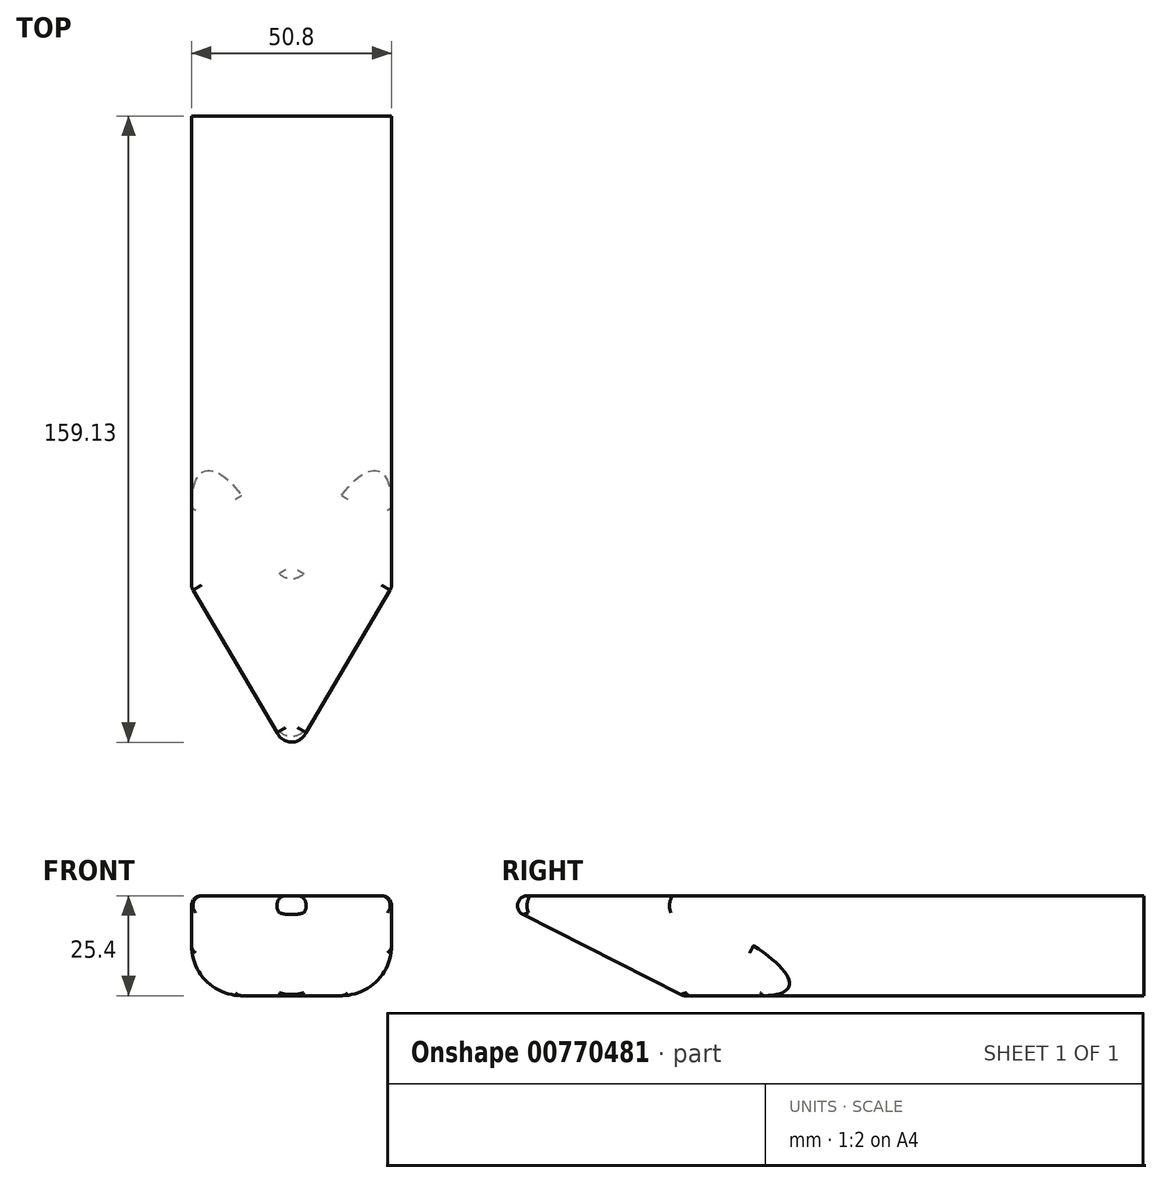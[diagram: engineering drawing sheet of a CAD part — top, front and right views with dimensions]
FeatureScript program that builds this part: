
annotation { "Feature Type Name" : "Feature", "Feature Type Description" : "" }
export const myFeature = defineFeature(function(context is Context, id is Id, definition is map)
    precondition{}
    {
        {
            var Q0;
            Q0=qCreatedBy(makeId("Top.planeOp"),FACE);
            var sketch = newSketch(context, id + "F0", { "sketchPlane" : qUnion([Q0])});
            skLineSegment(sketch, "E0.bottom", {"start": v(25.4, 63.5) * mm, "end": v(-25.4, 63.5) * mm});
            skLineSegment(sketch, "E0.top", {"start": v(25.4, -63.5) * mm, "end": v(-25.4, -63.5) * mm});
            skLineSegment(sketch, "E0.left", {"start": v(25.4, 63.5) * mm, "end": v(25.4, -63.5) * mm});
            skLineSegment(sketch, "E0.right", {"start": v(-25.4, 63.5) * mm, "end": v(-25.4, -63.5) * mm});
            skPoint(sketch, "E0.middle", {"position": v(0, 0) * mm});
            skLineSegment(sketch, "E1", {"start": v(-25.4, -63.5) * mm, "end": v(0, -106.64) * mm});
            skLineSegment(sketch, "E2", {"start": v(0, -106.64) * mm, "end": v(25.4, -63.5) * mm});
            skSolve(sketch);
        }
        {
            var Q0;
            Q0 = qSketchRegion(id + "F0", true);
            extrude(context, id + "F1", {"entities" : qUnion([Q0]), "depth" : 25.4 * mm, "offsetDistance" : 25.4 * mm});
        }
        {
            var Q0;
            Q0=makeQuery(id+"F1.opExtrude","CAP_EDGE",EDGE,{"disambiguationData":[OSD([sQuery(id+"F0.wireOp",EDGE,"E2")])],"isStart":true});
            var Q1;
            Q1=makeQuery(id+"F1.opExtrude","CAP_EDGE",EDGE,{"disambiguationData":[OSD([sQuery(id+"F0.wireOp",EDGE,"E1")])],"isStart":true});
            chamfer(context, id + "F2", {"entities" : qUnion([Q0, Q1]), "width" : 25.4 * mm, "tangentPropagation" : true});
        }
        {
            var Q0;
            Q0=makeQuery(id+"F2.opChamfer","BLEND_EDGE",EDGE,{"blendedFrom":[makeQuery(id+"F1.opExtrude","CAP_EDGE",EDGE,{"disambiguationData":[OSD([sQuery(id+"F0.wireOp",EDGE,"E1")])],"isStart":true}),makeQuery(id+"F1.opExtrude","CAP_EDGE",EDGE,{"disambiguationData":[OSD([sQuery(id+"F0.wireOp",EDGE,"E2")])],"isStart":true})],"blendedInto":[]});
            fillet(context, id + "F3", {"entities" : qUnion([Q0]), "radius" : 5.08 * mm, "tangentPropagation" : true, "allowEdgeOverflow" : false});
        }
        {
            var Q0;
            {var subQ0=sQuery(id+"F0.wireOp",EDGE,"E2");Q0=makeQuery(id+"F2.opChamfer","BLEND_EDGE",EDGE,{"blendedFrom":[makeQuery(id+"F1.opExtrude","CAP_EDGE",EDGE,{"disambiguationData":[OSD([subQ0])],"isStart":true}),makeQuery(id+"F1.opExtrude","CAP_FACE",FACE,{"disambiguationData":[OSD([sQuery(id+"F0.wireOp",EDGE,"E0.bottom"),sQuery(id+"F0.wireOp",EDGE,"E0.left"),sQuery(id+"F0.wireOp",EDGE,"E0.right"),sQuery(id+"F0.wireOp",EDGE,"E1"),subQ0])],"isStart":false})],"blendedInto":[makeQuery(id+"F1.opExtrude","CAP_FACE",FACE,{"disambiguationData":[OSD([sQuery(id+"F0.wireOp",EDGE,"E0.bottom"),sQuery(id+"F0.wireOp",EDGE,"E0.left"),sQuery(id+"F0.wireOp",EDGE,"E0.right"),sQuery(id+"F0.wireOp",EDGE,"E1"),subQ0])],"isStart":false})]});}
            var Q1;
            {var subQ0=sQuery(id+"F0.wireOp",EDGE,"E1");Q1=makeQuery(id+"F2.opChamfer","BLEND_EDGE",EDGE,{"blendedFrom":[makeQuery(id+"F1.opExtrude","CAP_EDGE",EDGE,{"disambiguationData":[OSD([subQ0])],"isStart":true}),makeQuery(id+"F1.opExtrude","CAP_FACE",FACE,{"disambiguationData":[OSD([sQuery(id+"F0.wireOp",EDGE,"E0.bottom"),sQuery(id+"F0.wireOp",EDGE,"E0.left"),sQuery(id+"F0.wireOp",EDGE,"E0.right"),subQ0,sQuery(id+"F0.wireOp",EDGE,"E2")])],"isStart":false})],"blendedInto":[makeQuery(id+"F1.opExtrude","CAP_FACE",FACE,{"disambiguationData":[OSD([sQuery(id+"F0.wireOp",EDGE,"E0.bottom"),sQuery(id+"F0.wireOp",EDGE,"E0.left"),sQuery(id+"F0.wireOp",EDGE,"E0.right"),subQ0,sQuery(id+"F0.wireOp",EDGE,"E2")])],"isStart":false})]});}
            fillet(context, id + "F4", {"entities" : qUnion([Q0, Q1]), "radius" : 2.54 * mm, "tangentPropagation" : true, "allowEdgeOverflow" : false});
        }
        {
            var Q0;
            {var subQ0=sQuery(id+"F0.wireOp",EDGE,"E1");Q0=makeQuery(id+"F2.opChamfer","BLEND_EDGE",EDGE,{"blendedFrom":[makeQuery(id+"F1.opExtrude","CAP_EDGE",EDGE,{"disambiguationData":[OSD([subQ0])],"isStart":true}),makeQuery(id+"F1.opExtrude","CAP_FACE",FACE,{"disambiguationData":[OSD([sQuery(id+"F0.wireOp",EDGE,"E0.bottom"),sQuery(id+"F0.wireOp",EDGE,"E0.left"),sQuery(id+"F0.wireOp",EDGE,"E0.right"),subQ0,sQuery(id+"F0.wireOp",EDGE,"E2")])],"isStart":true})],"blendedInto":[makeQuery(id+"F1.opExtrude","CAP_FACE",FACE,{"disambiguationData":[OSD([sQuery(id+"F0.wireOp",EDGE,"E0.bottom"),sQuery(id+"F0.wireOp",EDGE,"E0.left"),sQuery(id+"F0.wireOp",EDGE,"E0.right"),subQ0,sQuery(id+"F0.wireOp",EDGE,"E2")])],"isStart":true})]});}
            var Q1;
            {var subQ0=sQuery(id+"F0.wireOp",EDGE,"E2");Q1=makeQuery(id+"F2.opChamfer","BLEND_EDGE",EDGE,{"blendedFrom":[makeQuery(id+"F1.opExtrude","CAP_EDGE",EDGE,{"disambiguationData":[OSD([subQ0])],"isStart":true}),makeQuery(id+"F1.opExtrude","CAP_FACE",FACE,{"disambiguationData":[OSD([sQuery(id+"F0.wireOp",EDGE,"E0.bottom"),sQuery(id+"F0.wireOp",EDGE,"E0.left"),sQuery(id+"F0.wireOp",EDGE,"E0.right"),sQuery(id+"F0.wireOp",EDGE,"E1"),subQ0])],"isStart":true})],"blendedInto":[makeQuery(id+"F1.opExtrude","CAP_FACE",FACE,{"disambiguationData":[OSD([sQuery(id+"F0.wireOp",EDGE,"E0.bottom"),sQuery(id+"F0.wireOp",EDGE,"E0.left"),sQuery(id+"F0.wireOp",EDGE,"E0.right"),sQuery(id+"F0.wireOp",EDGE,"E1"),subQ0])],"isStart":true})]});}
            var Q2;
            Q2=makeQuery(id+"F2.opChamfer","BLEND_EDGE",EDGE,{"blendedFrom":[makeQuery(id+"F1.opExtrude","CAP_EDGE",EDGE,{"disambiguationData":[OSD([sQuery(id+"F0.wireOp",EDGE,"E2")])],"isStart":true}),makeQuery(id+"F1.opExtrude","SWEPT_FACE",FACE,{"disambiguationData":[OSD([sQuery(id+"F0.wireOp",EDGE,"E0.left")])]})],"blendedInto":[makeQuery(id+"F1.opExtrude","SWEPT_FACE",FACE,{"disambiguationData":[OSD([sQuery(id+"F0.wireOp",EDGE,"E0.left")])]})]});
            var Q3;
            Q3=makeQuery(id+"F2.opChamfer","BLEND_EDGE",EDGE,{"blendedFrom":[makeQuery(id+"F1.opExtrude","CAP_EDGE",EDGE,{"disambiguationData":[OSD([sQuery(id+"F0.wireOp",EDGE,"E1")])],"isStart":true}),makeQuery(id+"F1.opExtrude","SWEPT_FACE",FACE,{"disambiguationData":[OSD([sQuery(id+"F0.wireOp",EDGE,"E0.right")])]})],"blendedInto":[makeQuery(id+"F1.opExtrude","SWEPT_FACE",FACE,{"disambiguationData":[OSD([sQuery(id+"F0.wireOp",EDGE,"E0.right")])]})]});
            fillet(context, id + "F5", {"entities" : qUnion([Q0, Q1, Q2, Q3]), "radius" : 2.54 * mm, "tangentPropagation" : true, "allowEdgeOverflow" : false});
        }
        {
            var Q0;
            Q0=makeQuery(id+"F1.opExtrude","CAP_EDGE",EDGE,{"disambiguationData":[OSD([sQuery(id+"F0.wireOp",EDGE,"E0.left")])],"isStart":true});
            var Q1;
            Q1=makeQuery(id+"F1.opExtrude","CAP_EDGE",EDGE,{"disambiguationData":[OSD([sQuery(id+"F0.wireOp",EDGE,"E0.right")])],"isStart":true});
            fillet(context, id + "F6", {"entities" : qUnion([Q0, Q1]), "radius" : 12.7 * mm, "tangentPropagation" : true, "allowEdgeOverflow" : false});
        }
    });
